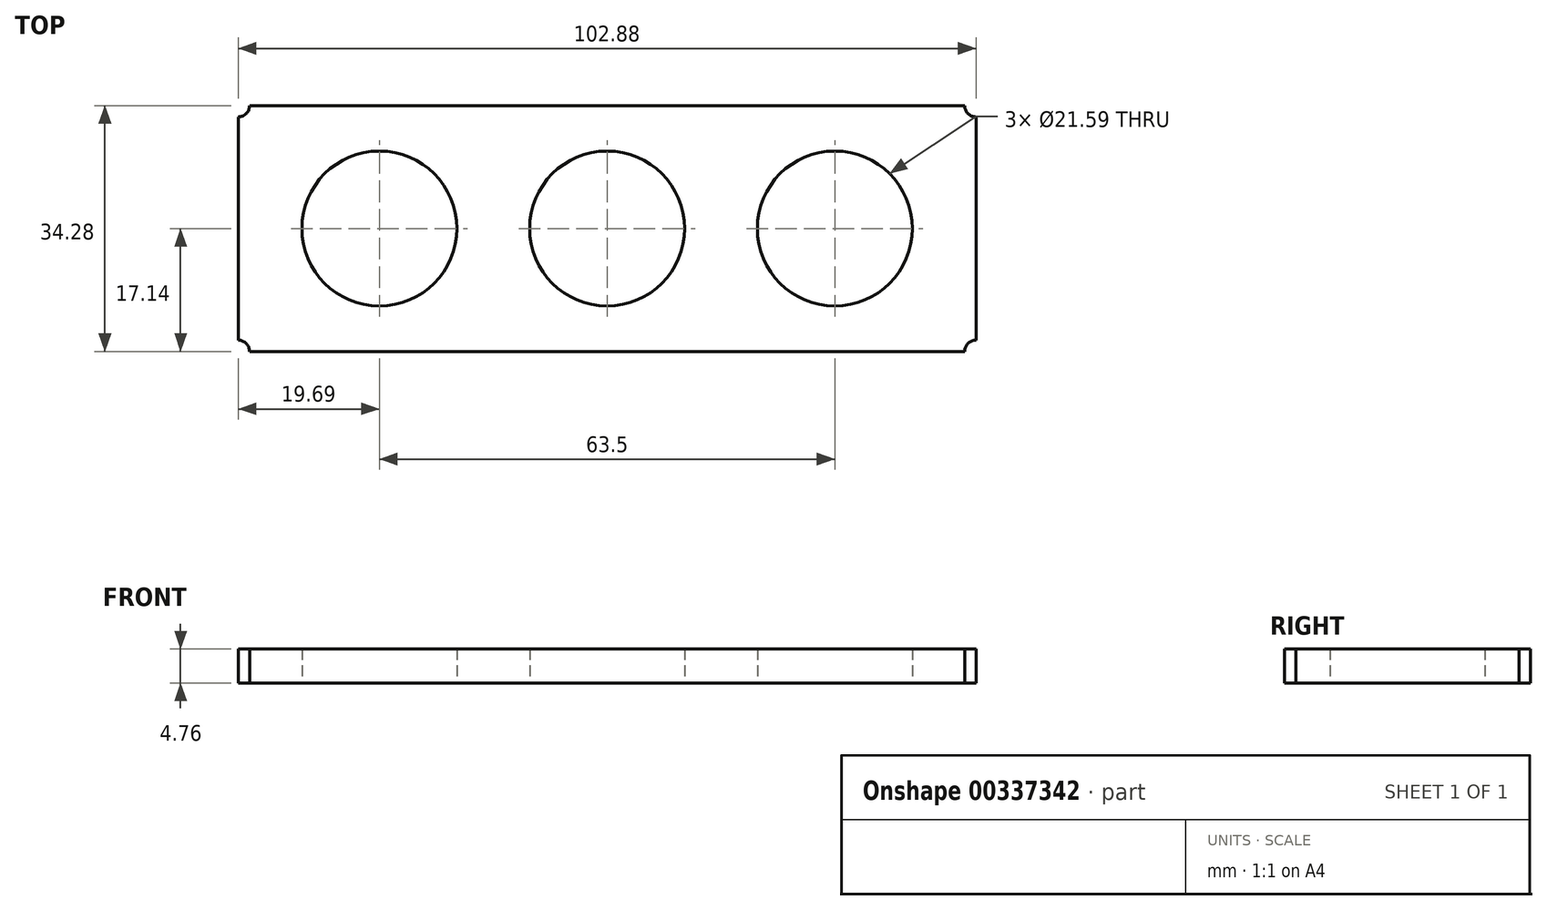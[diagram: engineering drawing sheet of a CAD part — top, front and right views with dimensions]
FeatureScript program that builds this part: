
annotation { "Feature Type Name" : "Feature", "Feature Type Description" : "" }
export const myFeature = defineFeature(function(context is Context, id is Id, definition is map)
    precondition{}
    {
        {
            var Q0;
            Q0=qCreatedBy(makeId("Top.planeOp"),FACE);
            var sketch = newSketch(context, id + "F0", { "sketchPlane" : qUnion([Q0])});
            skLineSegment(sketch, "E0.bottom", {"start": v(51.44, 17.15) * mm, "end": v(-51.44, 17.15) * mm});
            skLineSegment(sketch, "E0.top", {"start": v(51.44, -17.14) * mm, "end": v(-51.44, -17.14) * mm});
            skLineSegment(sketch, "E0.left", {"start": v(51.44, 17.15) * mm, "end": v(51.44, -17.14) * mm});
            skLineSegment(sketch, "E0.right", {"start": v(-51.44, 17.15) * mm, "end": v(-51.44, -17.15) * mm});
            skPoint(sketch, "E0.middle", {"position": v(0, 0) * mm});
            skCircle(sketch, "E1", {"center": v(-31.75, 0) * mm, "radius": 10.8 * mm});
            skCircle(sketch, "E2.1.0.0", {"center": v(0, 0) * mm, "radius": 10.8 * mm});
            skCircle(sketch, "E2.2.0.0", {"center": v(31.75, 0) * mm, "radius": 10.8 * mm});
            skLineSegment(sketch, "E2.direction1", {"start": v(-31.75, 0) * mm, "end": v(0, 0) * mm, "construction": true});
            skCircle(sketch, "E3", {"center": v(-51.44, 17.15) * mm, "radius": 1.59 * mm});
            skCircle(sketch, "E4", {"center": v(51.44, 17.15) * mm, "radius": 1.59 * mm});
            skCircle(sketch, "E5", {"center": v(51.44, -17.14) * mm, "radius": 1.59 * mm});
            skCircle(sketch, "E6", {"center": v(-51.44, -17.14) * mm, "radius": 1.59 * mm});
            skSolve(sketch);
        }
        {
            var Q0;
            Q0=makeQuery(id+"F0.imprint","IMPRINT",FACE,{"disambiguationData":[TD([[makeQuery(id+"F0.imprint","IMPRINT",EDGE,{"derivedFrom":sQuery(id+"F0.wireOp",EDGE,"E1")}),-1.0]])]});
            extrude(context, id + "F1", {"entities" : qUnion([Q0]), "depth" : 4.76 * mm});
        }
    });
